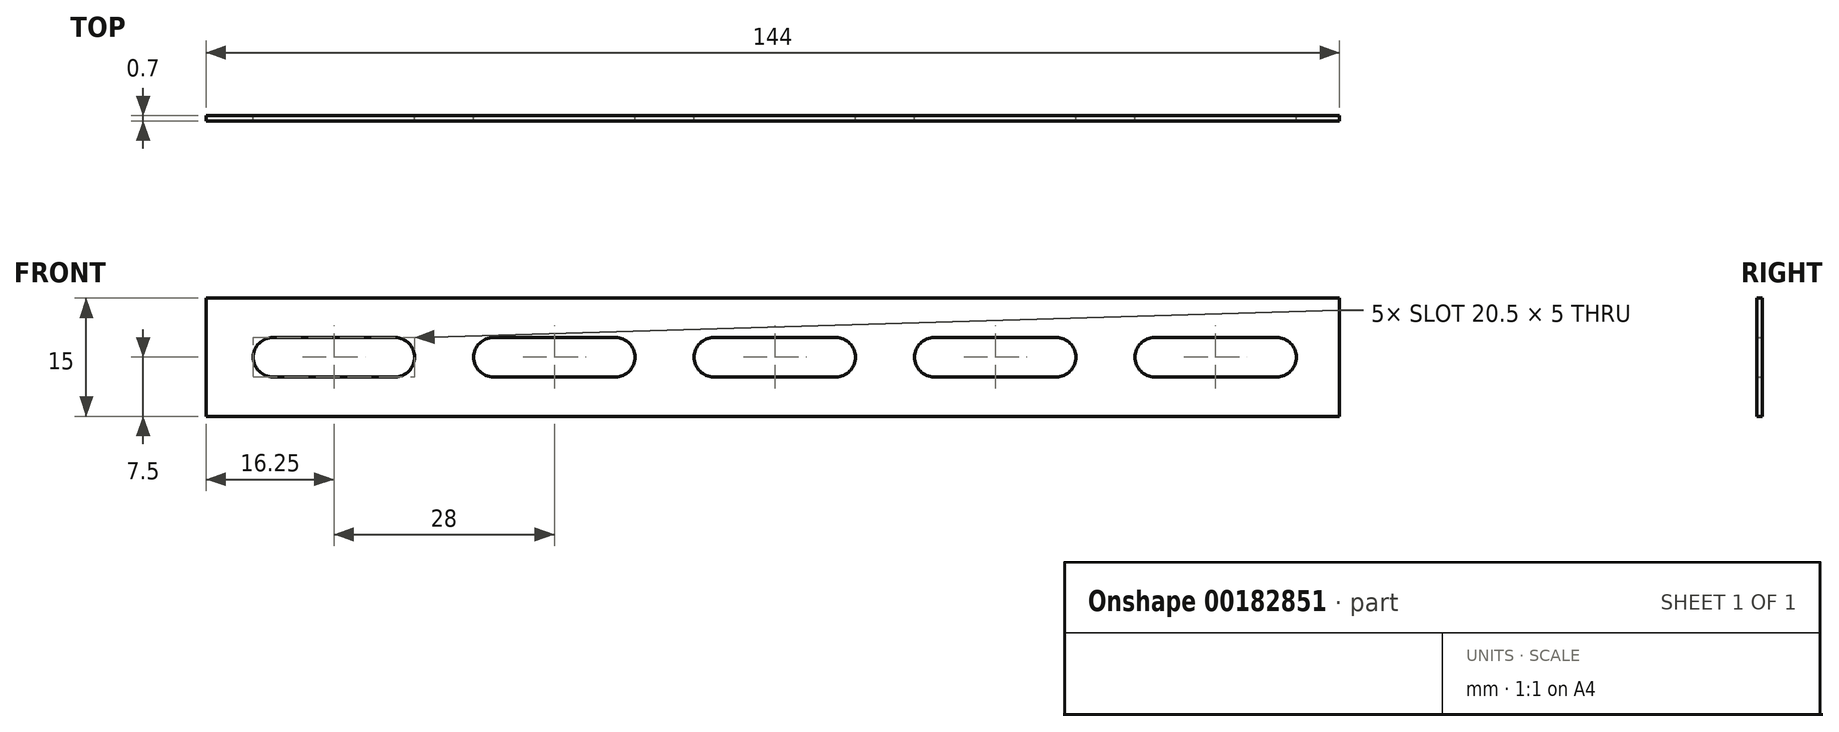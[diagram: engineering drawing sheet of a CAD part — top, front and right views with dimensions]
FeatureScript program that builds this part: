
annotation { "Feature Type Name" : "Feature", "Feature Type Description" : "" }
export const myFeature = defineFeature(function(context is Context, id is Id, definition is map)
    precondition{}
    {
        {
            var Q0;
            Q0=qCreatedBy(makeId("Front.planeOp"),FACE);
            var sketch = newSketch(context, id + "F0", { "sketchPlane" : qUnion([Q0])});
            skLineSegment(sketch, "E0.bottom", {"start": v(72, 7.5) * mm, "end": v(-72, 7.5) * mm});
            skLineSegment(sketch, "E0.top", {"start": v(72, -7.5) * mm, "end": v(-72, -7.5) * mm});
            skLineSegment(sketch, "E0.left", {"start": v(72, 7.5) * mm, "end": v(72, -7.5) * mm});
            skLineSegment(sketch, "E0.right", {"start": v(-72, 7.5) * mm, "end": v(-72, -7.5) * mm});
            skPoint(sketch, "E0.middle", {"position": v(0, 0) * mm});
            skArc(sketch, "E1", {"start": v(-63.5, 2.5) * mm, "mid": v(-66, 0) * mm, "end": v(-63.5, -2.5) * mm});
            skArc(sketch, "E2", {"start": v(-48, -2.5) * mm, "mid": v(-45.5, 0) * mm, "end": v(-48, 2.5) * mm});
            skLineSegment(sketch, "E3", {"start": v(-63.5, 2.5) * mm, "end": v(-48, 2.5) * mm});
            skLineSegment(sketch, "E4.MirrorCS", {"start": v(-63.5, -2.5) * mm, "end": v(-48, -2.5) * mm});
            skLineSegment(sketch, "E5.1.0.0", {"start": v(-35.5, 2.5) * mm, "end": v(-20, 2.5) * mm});
            skArc(sketch, "E5.1.0.1", {"start": v(-20, -2.5) * mm, "mid": v(-17.5, 0) * mm, "end": v(-20, 2.5) * mm});
            skLineSegment(sketch, "E5.1.0.2", {"start": v(-35.5, -2.5) * mm, "end": v(-20, -2.5) * mm});
            skArc(sketch, "E5.1.0.3", {"start": v(-35.5, 2.5) * mm, "mid": v(-38, 0) * mm, "end": v(-35.5, -2.5) * mm});
            skLineSegment(sketch, "E5.2.0.0", {"start": v(-7.5, 2.5) * mm, "end": v(8, 2.5) * mm});
            skArc(sketch, "E5.2.0.1", {"start": v(8, -2.5) * mm, "mid": v(10.5, 0) * mm, "end": v(8, 2.5) * mm});
            skLineSegment(sketch, "E5.2.0.2", {"start": v(-7.5, -2.5) * mm, "end": v(8, -2.5) * mm});
            skArc(sketch, "E5.2.0.3", {"start": v(-7.5, 2.5) * mm, "mid": v(-10, 0) * mm, "end": v(-7.5, -2.5) * mm});
            skLineSegment(sketch, "E5.3.0.0", {"start": v(20.5, 2.5) * mm, "end": v(36, 2.5) * mm});
            skArc(sketch, "E5.3.0.1", {"start": v(36, -2.5) * mm, "mid": v(38.5, 0) * mm, "end": v(36, 2.5) * mm});
            skLineSegment(sketch, "E5.3.0.2", {"start": v(20.5, -2.5) * mm, "end": v(36, -2.5) * mm});
            skArc(sketch, "E5.3.0.3", {"start": v(20.5, 2.5) * mm, "mid": v(18, 0) * mm, "end": v(20.5, -2.5) * mm});
            skLineSegment(sketch, "E5.4.0.0", {"start": v(48.5, 2.5) * mm, "end": v(64, 2.5) * mm});
            skArc(sketch, "E5.4.0.1", {"start": v(64, -2.5) * mm, "mid": v(66.5, 0) * mm, "end": v(64, 2.5) * mm});
            skLineSegment(sketch, "E5.4.0.2", {"start": v(48.5, -2.5) * mm, "end": v(64, -2.5) * mm});
            skArc(sketch, "E5.4.0.3", {"start": v(48.5, 2.5) * mm, "mid": v(46, 0) * mm, "end": v(48.5, -2.5) * mm});
            skLineSegment(sketch, "E5.direction1", {"start": v(-63.5, 2.5) * mm, "end": v(-35.5, 2.5) * mm, "construction": true});
            skSolve(sketch);
        }
        {
            var Q0;
            Q0 = qSketchRegion(id + "F0", true);
            extrude(context, id + "F1", {"entities" : qUnion([Q0]), "endBound" : BoundingType.SYMMETRIC, "depth" : 0.7 * mm});
        }
    });
